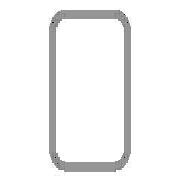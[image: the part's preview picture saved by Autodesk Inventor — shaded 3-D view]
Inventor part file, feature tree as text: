
AUTODESK INVENTOR PART (.ipt)
format: ipt  version: 2025 (Build 290162010, 162A)  size: 152,576 bytes
history: native  units: mm (DEFAULTED — no unit token found)
features: other x4, plane x3, split x2, sketch x1
ambient origin geometry x8: Origin, YZ Plane, XZ Plane, XY Plane, X Axis, Y Axis, Z Axis, Center Point
bodies: Solid1 (feature_tree), Body (feature_tree)
feature tree (10):
  parser-record x1  (decoder bookkeeping rows leaked as tree rows — omitted from the tree; the rows remain in map.json)
  other  "Driven Length"
  other  "Start Plane"
  other  "End Plane"
  plane  "Work Plane4"
  split  "Split1"
  plane  "Work Plane5"
  split  "Split2"
  sketch  "Sketch3"  dims[d3=615.253612mm d4=0.0mm d7=4.0mm d9=20.0mm d11=40.0mm d12=2.0mm d13=-6.618856mm d14=608.634757mm d15=10.0mm d16=20.0mm d17=90.0deg d18=615.253612mm]
  plane  "Work Plane3"
